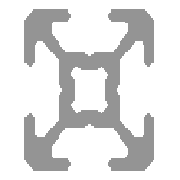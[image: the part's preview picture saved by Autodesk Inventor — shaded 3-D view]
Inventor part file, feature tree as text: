
AUTODESK INVENTOR PART (.ipt)
format: ipt  version: 2015 (Build 190159000, 159)  size: 372,224 bytes
history: native  units: mm
features: other x3, extrude x1, sketch x1
ambient origin geometry x8: Origin, YZ Plane, XZ Plane, XY Plane, X Axis, Y Axis, Z Axis, Center Point
bodies: Body1 (feature_tree)
feature tree (5):
  other  "Blocks"
  extrude  "Extrusion3"  [1 undecoded]
  sketch  "Sketch1"  dims[d23=0.0mm]
  other  "20x20"
  other  "20x20:1"
note: 1 required parameter value undecoded (feature->parameter linkage not recoverable at this tier; creation-order binding heuristic only, values carry confidence <= 0.55)
